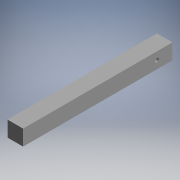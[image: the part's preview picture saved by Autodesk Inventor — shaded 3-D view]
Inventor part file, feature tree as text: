
AUTODESK INVENTOR PART (.ipt)
format: ipt  version: 2019 (Build 230136000, 136)  size: 96,256 bytes
history: native  units: mm (DEFAULTED — no unit token found)
features: extrude x2, sketch x2
ambient origin geometry x8: Origin, YZ Plane, XZ Plane, XY Plane, X Axis, Y Axis, Z Axis, Center Point
bodies: Solid1 (feature_tree)
feature tree (4):
  extrude  "Extrusion1"  Depth=31.75mm
  extrude  "Extrusion2"  Depth=31.75mm
  sketch  "Sketch1"  dims[d0=31.75mm d1=31.75mm]
  sketch  "Sketch2"  dims[d2=304.8mm d3=0.0mm d4=31.75mm d5=31.75mm d6=15.875mm d7=7.62mm d8=120.0mm d9=0.0mm]
